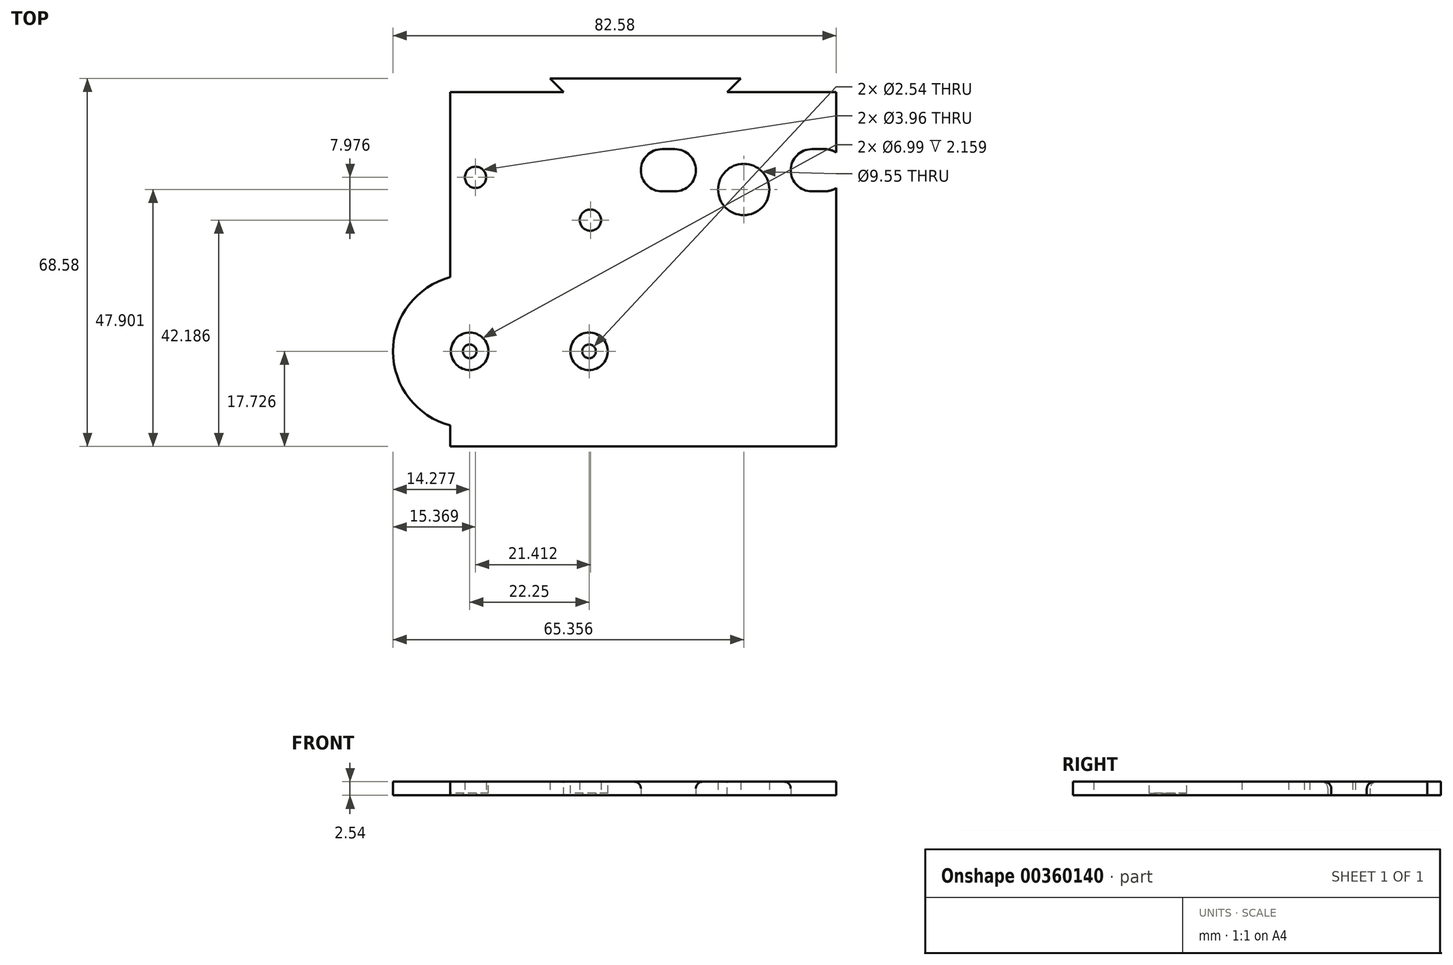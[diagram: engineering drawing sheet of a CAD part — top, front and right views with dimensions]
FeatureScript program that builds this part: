
annotation { "Feature Type Name" : "Feature", "Feature Type Description" : "" }
export const myFeature = defineFeature(function(context is Context, id is Id, definition is map)
    precondition{}
    {
        {
            var Q0;
            Q0=qCreatedBy(makeId("Top.planeOp"),FACE);
            var sketch = newSketch(context, id + "F0", { "sketchPlane" : qUnion([Q0])});
            skLineSegment(sketch, "E0.bottom", {"start": v(0, 0) * mm, "end": v(71.9, 0) * mm, "construction": true});
            skLineSegment(sketch, "E0.top", {"start": v(0, 33.43) * mm, "end": v(71.9, 33.43) * mm});
            skLineSegment(sketch, "E0.left", {"start": v(0, 0) * mm, "end": v(0, 33.43) * mm});
            skLineSegment(sketch, "E0.right", {"start": v(71.9, 0) * mm, "end": v(71.9, 33.43) * mm});
            skLineSegment(sketch, "E1.bottom", {"start": v(0, 0) * mm, "end": v(71.9, 0) * mm});
            skLineSegment(sketch, "E1.top", {"start": v(0, -32.61) * mm, "end": v(71.9, -32.61) * mm});
            skLineSegment(sketch, "E1.left", {"start": v(0, 0) * mm, "end": v(0, -32.61) * mm});
            skLineSegment(sketch, "E1.right", {"start": v(71.9, 0) * mm, "end": v(71.9, -32.61) * mm});
            skCircle(sketch, "E2", {"center": v(54.69, 15.3) * mm, "radius": 4.78 * mm});
            skPoint(sketch, "E2.centerSnap0", {"position": v(71.9, 16.71) * mm});
            skCircle(sketch, "E3", {"center": v(4.7, 17.55) * mm, "radius": 1.98 * mm});
            skCircle(sketch, "E4", {"center": v(26.11, 9.58) * mm, "radius": 1.98 * mm});
            skLineSegment(sketch, "E5.left", {"start": v(3.6, -29.16) * mm, "end": v(3.6, -0.6) * mm, "construction": true});
            skArc(sketch, "E6", {"start": v(3.6, -0.6) * mm, "mid": v(-10.67, -14.88) * mm, "end": v(3.6, -29.16) * mm, "construction": true});
            skCircle(sketch, "E7", {"center": v(3.6, -14.88) * mm, "radius": 1.27 * mm});
            skCircle(sketch, "E8", {"center": v(25.86, -14.88) * mm, "radius": 1.27 * mm});
            skArc(sketch, "E9", {"start": v(0, -1.07) * mm, "mid": v(-10.67, -14.88) * mm, "end": v(0, -28.7) * mm});
            skLineSegment(sketch, "E10", {"start": v(3.6, -14.88) * mm, "end": v(71.9, -14.88) * mm, "construction": true});
            skSolve(sketch);
        }
        {
            var Q0;
            Q0=makeQuery(id+"F0.imprint","IMPRINT",FACE,{"disambiguationData":[TD([[makeQuery(id+"F0.imprint","IMPRINT",EDGE,{"derivedFrom":sQuery(id+"F0.wireOp",EDGE,"E0.top")}),-1.0]])]});
            var Q1;
            Q1=makeQuery(id+"F0.imprint","IMPRINT",FACE,{"disambiguationData":[TD([[makeQuery(id+"F0.imprint","IMPRINT",EDGE,{"derivedFrom":sQuery(id+"F0.wireOp",EDGE,"E1.bottom")}),-1.0]])]});
            var Q2;
            {var subQ0=sQuery(id+"F0.wireOp",EDGE,"E9");Q2=makeQuery(id+"F0.imprint","IMPRINT",FACE,{"disambiguationData":[TD([[makeQuery(id+"F0.imprint","IMPRINT",EDGE,{"derivedFrom":subQ0}),1.0]])]});}
            extrude(context, id + "F1", {"entities" : qUnion([Q0, Q1, Q2]), "depth" : 2.54 * mm});
        }
        {
            var Q0;
            Q0=makeQuery(id+"F0.imprint","IMPRINT",FACE,{"disambiguationData":[TD([[makeQuery(id+"F0.imprint","IMPRINT",EDGE,{"derivedFrom":sQuery(id+"F0.wireOp",EDGE,"E0.top")}),-1.0]])]});
            var sketch = newSketch(context, id + "F2", { "sketchPlane" : qUnion([Q0])});
            skLineSegment(sketch, "E11.bottom", {"start": v(69.77, 22.81) * mm, "end": v(67.39, 22.81) * mm});
            skLineSegment(sketch, "E11.top", {"start": v(69.77, 14.94) * mm, "end": v(67.39, 14.94) * mm});
            skLineSegment(sketch, "E11.left", {"start": v(73.71, 18.87) * mm, "end": v(73.71, 18.87) * mm});
            skLineSegment(sketch, "E11.right", {"start": v(63.45, 18.87) * mm, "end": v(63.45, 18.87) * mm});
            skLineSegment(sketch, "E12.bottom", {"start": v(41.83, 22.81) * mm, "end": v(39.45, 22.81) * mm});
            skLineSegment(sketch, "E12.top", {"start": v(41.83, 14.94) * mm, "end": v(39.45, 14.94) * mm});
            skLineSegment(sketch, "E12.left", {"start": v(45.77, 18.87) * mm, "end": v(45.77, 18.87) * mm});
            skLineSegment(sketch, "E12.right", {"start": v(35.5, 18.87) * mm, "end": v(35.5, 18.87) * mm});
            skPoint(sketch, "E13.visualSharp", {"position": v(63.45, 22.81) * mm});
            skArc(sketch, "E13.filletArc", {"start": v(67.39, 22.81) * mm, "mid": v(64.6, 21.66) * mm, "end": v(63.45, 18.87) * mm});
            skPoint(sketch, "E14.visualSharp", {"position": v(63.45, 14.94) * mm});
            skArc(sketch, "E14.filletArc", {"start": v(63.45, 18.87) * mm, "mid": v(64.6, 16.09) * mm, "end": v(67.39, 14.94) * mm});
            skPoint(sketch, "E15.visualSharp", {"position": v(73.71, 22.81) * mm});
            skArc(sketch, "E15.filletArc", {"start": v(73.71, 18.87) * mm, "mid": v(72.56, 21.66) * mm, "end": v(69.77, 22.81) * mm});
            skPoint(sketch, "E16.visualSharp", {"position": v(73.71, 14.94) * mm});
            skArc(sketch, "E16.filletArc", {"start": v(69.77, 14.94) * mm, "mid": v(72.56, 16.09) * mm, "end": v(73.71, 18.87) * mm});
            skPoint(sketch, "E17.visualSharp", {"position": v(45.77, 22.81) * mm});
            skArc(sketch, "E17.filletArc", {"start": v(45.77, 18.87) * mm, "mid": v(44.62, 21.66) * mm, "end": v(41.83, 22.81) * mm});
            skPoint(sketch, "E18.visualSharp", {"position": v(45.77, 14.94) * mm});
            skArc(sketch, "E18.filletArc", {"start": v(41.83, 14.94) * mm, "mid": v(44.62, 16.09) * mm, "end": v(45.77, 18.87) * mm});
            skPoint(sketch, "E19.visualSharp", {"position": v(35.5, 14.94) * mm});
            skArc(sketch, "E19.filletArc", {"start": v(35.5, 18.87) * mm, "mid": v(36.66, 16.09) * mm, "end": v(39.45, 14.94) * mm});
            skPoint(sketch, "E20.visualSharp", {"position": v(35.5, 22.81) * mm});
            skArc(sketch, "E20.filletArc", {"start": v(39.45, 22.81) * mm, "mid": v(36.66, 21.66) * mm, "end": v(35.5, 18.87) * mm});
            skLineSegment(sketch, "E21", {"start": v(67.39, 22.81) * mm, "end": v(41.83, 22.81) * mm, "construction": true});
            skSolve(sketch);
        }
        {
            var Q0;
            Q0 = qSketchRegion(id + "F2", true);
            extrude(context, id + "F3", {"entities" : qUnion([Q0]), "operationType" : NewBodyOperationType.REMOVE, "depth" : 25.4 * mm});
        }
        {
            var Q0;
            Q0=makeQuery(id+"F1.opExtrude","SWEPT_FACE",FACE,{"disambiguationData":[OSD([sQuery(id+"F0.wireOp",EDGE,"E0.top")])]});
            var sketch = newSketch(context, id + "F4", { "sketchPlane" : qUnion([Q0])});
            skLineSegment(sketch, "E22", {"start": v(-18.57, 2.54) * mm, "end": v(-18.57, 0) * mm});
            skLineSegment(sketch, "E23", {"start": v(-54.13, 2.54) * mm, "end": v(-54.13, 0) * mm});
            skSolve(sketch);
        }
        {
            var Q0;
            {var subQ0=sQuery(id+"F4.wireOp",EDGE,"E22");Q0=makeQuery(id+"F4.imprint","IMPRINT",FACE,{"disambiguationData":[TD([[makeQuery(id+"F4.imprint","IMPRINT",EDGE,{"derivedFrom":subQ0}),-1.0]])]});}
            extrude(context, id + "F5", {"entities" : qUnion([Q0]), "operationType" : NewBodyOperationType.ADD, "depth" : 2.54 * mm});
        }
        {
            var Q0;
            {var subQ0=sQuery(id+"F0.wireOp",EDGE,"E0.top");var subQ1=makeQuery(id+"F1.opExtrude","CAP_EDGE",EDGE,{"disambiguationData":[OSD([subQ0])],"isStart":false});Q0=makeQuery(id+"F5.boolean.opBoolean","MERGE",FACE,{"derivedFrom":[makeQuery(id+"F1.opExtrude","CAP_FACE",FACE,{"disambiguationData":[OSD([subQ0,sQuery(id+"F0.wireOp",EDGE,"E0.left"),sQuery(id+"F0.wireOp",EDGE,"E0.right"),sQuery(id+"F0.wireOp",EDGE,"E1.top"),sQuery(id+"F0.wireOp",EDGE,"E1.left"),sQuery(id+"F0.wireOp",EDGE,"E1.right"),sQuery(id+"F0.wireOp",EDGE,"E2"),sQuery(id+"F0.wireOp",EDGE,"E3"),sQuery(id+"F0.wireOp",EDGE,"E4"),sQuery(id+"F0.wireOp",EDGE,"E7"),sQuery(id+"F0.wireOp",EDGE,"E8"),sQuery(id+"F0.wireOp",EDGE,"E9")])],"isStart":false}),makeQuery(id+"F5.opExtrude","SWEPT_FACE",FACE,{"disambiguationData":[OSD([subQ0]),TDD([makeQuery(id+"F4.imprint","IMPRINT",EDGE,{"disambiguationData":[TD([[makeQuery(id+"F4.imprint","INTERSECT",VERTEX,{"derivedFrom":[subQ1,sQuery(id+"F4.wireOp",EDGE,"E22")]}),-1.0]])],"derivedFrom":subQ1})])]})]});}
            var sketch = newSketch(context, id + "F6", { "sketchPlane" : qUnion([Q0])});
            skLineSegment(sketch, "E24", {"start": v(21.1, 33.43) * mm, "end": v(18.57, 35.97) * mm});
            skLineSegment(sketch, "E25", {"start": v(54.13, 35.97) * mm, "end": v(51.59, 33.43) * mm});
            skLineSegment(sketch, "E26", {"start": v(18.57, 33.43) * mm, "end": v(54.13, 33.43) * mm, "construction": true});
            skLineSegment(sketch, "E27", {"start": v(18.57, 33.43) * mm, "end": v(21.1, 33.43) * mm});
            skLineSegment(sketch, "E28", {"start": v(51.59, 33.43) * mm, "end": v(54.13, 33.43) * mm});
            skSolve(sketch);
        }
        {
            var Q0;
            Q0=makeQuery(id+"F6.imprint","IMPRINT",FACE,{"disambiguationData":[TD([[makeQuery(id+"F6.imprint","IMPRINT",EDGE,{"derivedFrom":sQuery(id+"F6.wireOp",EDGE,"E24")}),1.0]])]});
            var Q1;
            Q1=makeQuery(id+"F6.imprint","IMPRINT",FACE,{"disambiguationData":[TD([[makeQuery(id+"F6.imprint","IMPRINT",EDGE,{"derivedFrom":sQuery(id+"F6.wireOp",EDGE,"E25")}),1.0]])]});
            extrude(context, id + "F7", {"entities" : qUnion([Q0, Q1]), "operationType" : NewBodyOperationType.REMOVE, "oppositeDirection" : true, "depth" : 2.54 * mm});
        }
        {
            var Q0;
            {var subQ0=sQuery(id+"F0.wireOp",EDGE,"E0.top");var subQ1=makeQuery(id+"F1.opExtrude","CAP_EDGE",EDGE,{"disambiguationData":[OSD([subQ0])],"isStart":false});Q0=makeQuery(id+"F5.boolean.opBoolean","MERGE",FACE,{"derivedFrom":[makeQuery(id+"F1.opExtrude","CAP_FACE",FACE,{"disambiguationData":[OSD([subQ0,sQuery(id+"F0.wireOp",EDGE,"E0.left"),sQuery(id+"F0.wireOp",EDGE,"E0.right"),sQuery(id+"F0.wireOp",EDGE,"E1.top"),sQuery(id+"F0.wireOp",EDGE,"E1.left"),sQuery(id+"F0.wireOp",EDGE,"E1.right"),sQuery(id+"F0.wireOp",EDGE,"E2"),sQuery(id+"F0.wireOp",EDGE,"E3"),sQuery(id+"F0.wireOp",EDGE,"E4"),sQuery(id+"F0.wireOp",EDGE,"E7"),sQuery(id+"F0.wireOp",EDGE,"E8"),sQuery(id+"F0.wireOp",EDGE,"E9")])],"isStart":false}),makeQuery(id+"F5.opExtrude","SWEPT_FACE",FACE,{"disambiguationData":[OSD([subQ0]),TDD([makeQuery(id+"F4.imprint","IMPRINT",EDGE,{"disambiguationData":[TD([[makeQuery(id+"F4.imprint","INTERSECT",VERTEX,{"derivedFrom":[subQ1,sQuery(id+"F4.wireOp",EDGE,"E22")]}),-1.0]])],"derivedFrom":subQ1})])]})]});}
            var sketch = newSketch(context, id + "F8", { "sketchPlane" : qUnion([Q0])});
            skCircle(sketch, "E29", {"center": v(3.6, -14.88) * mm, "radius": 3.5 * mm});
            skCircle(sketch, "E30", {"center": v(25.86, -14.88) * mm, "radius": 3.5 * mm});
            skSolve(sketch);
        }
        {
            var Q0;
            Q0=makeQuery(id+"F8.imprint","IMPRINT",FACE,{"disambiguationData":[TD([[makeQuery(id+"F8.imprint","IMPRINT",EDGE,{"derivedFrom":sQuery(id+"F8.wireOp",EDGE,"E29")}),1.0]])]});
            var Q1;
            Q1=makeQuery(id+"F8.imprint","IMPRINT",FACE,{"disambiguationData":[TD([[makeQuery(id+"F8.imprint","IMPRINT",EDGE,{"derivedFrom":sQuery(id+"F8.wireOp",EDGE,"E30")}),1.0]])]});
            extrude(context, id + "F9", {"entities" : qUnion([Q0, Q1]), "operationType" : NewBodyOperationType.REMOVE, "oppositeDirection" : true, "depth" : 2.16 * mm});
        }
        {
            var Q0;
            Q0=makeQuery(id+"F3.boolean.opBoolean","INTERSECT",EDGE,{"derivedFrom":[makeQuery(id+"F1.opExtrude","CAP_FACE",FACE,{"disambiguationData":[OSD([sQuery(id+"F0.wireOp",EDGE,"E0.top"),sQuery(id+"F0.wireOp",EDGE,"E0.left"),sQuery(id+"F0.wireOp",EDGE,"E0.right"),sQuery(id+"F0.wireOp",EDGE,"E1.top"),sQuery(id+"F0.wireOp",EDGE,"E1.left"),sQuery(id+"F0.wireOp",EDGE,"E1.right"),sQuery(id+"F0.wireOp",EDGE,"E2"),sQuery(id+"F0.wireOp",EDGE,"E3"),sQuery(id+"F0.wireOp",EDGE,"E4"),sQuery(id+"F0.wireOp",EDGE,"E7"),sQuery(id+"F0.wireOp",EDGE,"E8"),sQuery(id+"F0.wireOp",EDGE,"E9")])],"isStart":false}),makeQuery(id+"F3.opExtrude","SWEPT_FACE",FACE,{"disambiguationData":[OSD([sQuery(id+"F2.wireOp",EDGE,"E19.filletArc"),sQuery(id+"F2.wireOp",EDGE,"E20.filletArc")])]})]});
            var Q1;
            Q1=makeQuery(id+"F3.boolean.opBoolean","INTERSECT",EDGE,{"derivedFrom":[makeQuery(id+"F1.opExtrude","CAP_FACE",FACE,{"disambiguationData":[OSD([sQuery(id+"F0.wireOp",EDGE,"E0.top"),sQuery(id+"F0.wireOp",EDGE,"E0.left"),sQuery(id+"F0.wireOp",EDGE,"E0.right"),sQuery(id+"F0.wireOp",EDGE,"E1.top"),sQuery(id+"F0.wireOp",EDGE,"E1.left"),sQuery(id+"F0.wireOp",EDGE,"E1.right"),sQuery(id+"F0.wireOp",EDGE,"E2"),sQuery(id+"F0.wireOp",EDGE,"E3"),sQuery(id+"F0.wireOp",EDGE,"E4"),sQuery(id+"F0.wireOp",EDGE,"E7"),sQuery(id+"F0.wireOp",EDGE,"E8"),sQuery(id+"F0.wireOp",EDGE,"E9")])],"isStart":false}),makeQuery(id+"F3.opExtrude","SWEPT_FACE",FACE,{"disambiguationData":[OSD([sQuery(id+"F2.wireOp",EDGE,"E13.filletArc"),sQuery(id+"F2.wireOp",EDGE,"E14.filletArc")])]})]});
            var Q2;
            Q2=makeQuery(id+"F3.boolean.opBoolean","COPY",EDGE,{"derivedFrom":makeQuery(id+"F3.opExtrude","CAP_EDGE",EDGE,{"disambiguationData":[OSD([sQuery(id+"F2.wireOp",EDGE,"E13.filletArc"),sQuery(id+"F2.wireOp",EDGE,"E14.filletArc")])],"isStart":true})});
            var Q3;
            Q3=makeQuery(id+"F3.boolean.opBoolean","COPY",EDGE,{"derivedFrom":makeQuery(id+"F3.opExtrude","CAP_EDGE",EDGE,{"disambiguationData":[OSD([sQuery(id+"F2.wireOp",EDGE,"E17.filletArc"),sQuery(id+"F2.wireOp",EDGE,"E18.filletArc")])],"isStart":true})});
            fillet(context, id + "F10", {"entities" : qUnion([Q0, Q1, Q2, Q3]), "radius" : 1.27 * mm, "tangentPropagation" : true, "allowEdgeOverflow" : false});
        }
    });
